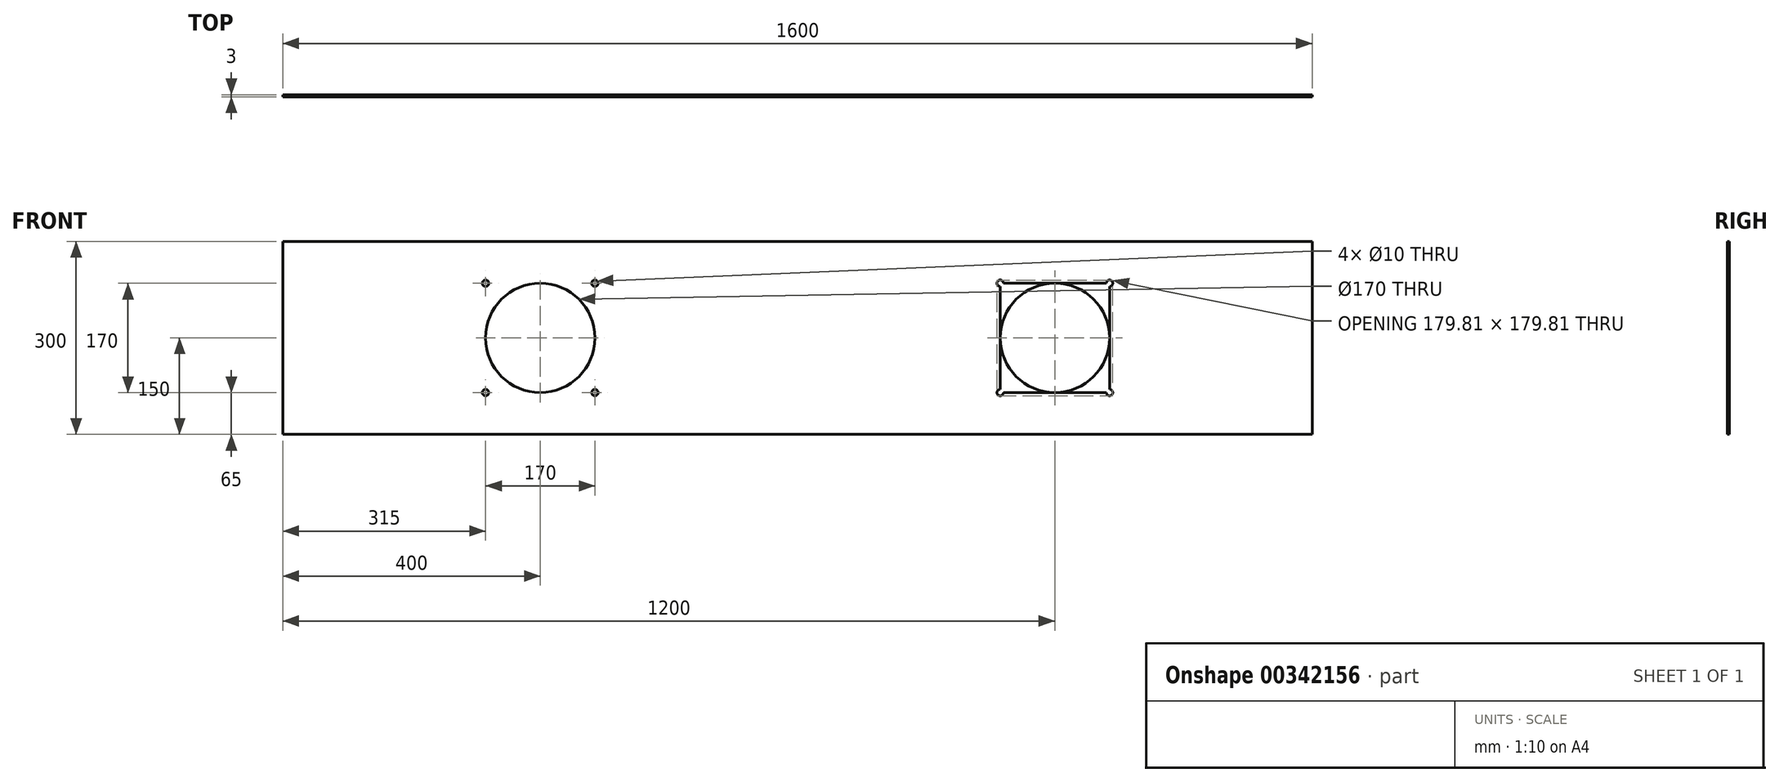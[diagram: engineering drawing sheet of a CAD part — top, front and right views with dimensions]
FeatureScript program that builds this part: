
annotation { "Feature Type Name" : "Feature", "Feature Type Description" : "" }
export const myFeature = defineFeature(function(context is Context, id is Id, definition is map)
    precondition{}
    {
        {
            var Q0;
            Q0=qCreatedBy(makeId("Front.planeOp"),FACE);
            var sketch = newSketch(context, id + "F0", { "sketchPlane" : qUnion([Q0])});
            skLineSegment(sketch, "E0.bottom", {"start": v(-800, 150) * mm, "end": v(800, 150) * mm});
            skLineSegment(sketch, "E0.top", {"start": v(-800, -150) * mm, "end": v(800, -150) * mm});
            skLineSegment(sketch, "E0.left", {"start": v(-800, 150) * mm, "end": v(-800, -150) * mm});
            skLineSegment(sketch, "E0.right", {"start": v(800, 150) * mm, "end": v(800, -150) * mm});
            skPoint(sketch, "E0.middle", {"position": v(0, 0) * mm});
            skCircle(sketch, "E1", {"center": v(-400, 0) * mm, "radius": 85 * mm});
            skCircle(sketch, "E2.MirrorC", {"center": v(400, 0) * mm, "radius": 85 * mm});
            skLineSegment(sketch, "E3.bottom", {"start": v(-315, 85) * mm, "end": v(-485, 85) * mm});
            skLineSegment(sketch, "E3.top", {"start": v(-315, -85) * mm, "end": v(-485, -85) * mm});
            skLineSegment(sketch, "E3.left", {"start": v(-315, 85) * mm, "end": v(-315, -85) * mm});
            skLineSegment(sketch, "E3.right", {"start": v(-485, 85) * mm, "end": v(-485, -85) * mm});
            skLineSegment(sketch, "E4.bottom", {"start": v(485, 85) * mm, "end": v(315, 85) * mm});
            skLineSegment(sketch, "E4.top", {"start": v(485, -85) * mm, "end": v(315, -85) * mm});
            skLineSegment(sketch, "E4.left", {"start": v(485, 85) * mm, "end": v(485, -85) * mm});
            skLineSegment(sketch, "E4.right", {"start": v(315, 85) * mm, "end": v(315, -85) * mm});
            skCircle(sketch, "E5", {"center": v(-485, 85) * mm, "radius": 5 * mm});
            skCircle(sketch, "E6", {"center": v(-315, 85) * mm, "radius": 5 * mm});
            skCircle(sketch, "E7", {"center": v(-485, -85) * mm, "radius": 5 * mm});
            skCircle(sketch, "E8", {"center": v(-315, -85) * mm, "radius": 5 * mm});
            skCircle(sketch, "E9", {"center": v(315, 85) * mm, "radius": 5 * mm});
            skCircle(sketch, "E10", {"center": v(485, 85) * mm, "radius": 5 * mm});
            skCircle(sketch, "E11", {"center": v(315, -85) * mm, "radius": 5 * mm});
            skCircle(sketch, "E12", {"center": v(485, -85) * mm, "radius": 5 * mm});
            skSolve(sketch);
        }
        {
            var Q0;
            Q0=makeQuery(id+"F0.imprint","IMPRINT",FACE,{"disambiguationData":[TD([[makeQuery(id+"F0.imprint","IMPRINT",EDGE,{"derivedFrom":sQuery(id+"F0.wireOp",EDGE,"E0.bottom")}),-1.0]])]});
            var Q1;
            {var subQ0=sQuery(id+"F0.wireOp",EDGE,"E3.bottom");var subQ1=sQuery(id+"F0.wireOp",EDGE,"E1");var subQ2=makeQuery(id+"F0.imprint","INTERSECT",VERTEX,{"derivedFrom":[subQ1,subQ0]});Q1=makeQuery(id+"F0.imprint","IMPRINT",FACE,{"disambiguationData":[TD([[makeQuery(id+"F0.imprint","IMPRINT",EDGE,{"disambiguationData":[TD([[subQ2,-1.0]])],"derivedFrom":subQ1}),-1.0]])]});}
            var Q2;
            {var subQ0=sQuery(id+"F0.wireOp",EDGE,"E3.bottom");var subQ1=sQuery(id+"F0.wireOp",EDGE,"E1");var subQ2=makeQuery(id+"F0.imprint","INTERSECT",VERTEX,{"derivedFrom":[subQ1,subQ0]});Q2=makeQuery(id+"F0.imprint","IMPRINT",FACE,{"disambiguationData":[TD([[makeQuery(id+"F0.imprint","IMPRINT",EDGE,{"disambiguationData":[TD([[subQ2,1.0]])],"derivedFrom":subQ1}),-1.0]])]});}
            var Q3;
            {var subQ0=sQuery(id+"F0.wireOp",EDGE,"E3.right");var subQ1=sQuery(id+"F0.wireOp",EDGE,"E1");var subQ2=makeQuery(id+"F0.imprint","INTERSECT",VERTEX,{"derivedFrom":[subQ1,subQ0]});Q3=makeQuery(id+"F0.imprint","IMPRINT",FACE,{"disambiguationData":[TD([[makeQuery(id+"F0.imprint","IMPRINT",EDGE,{"disambiguationData":[TD([[subQ2,-1.0]])],"derivedFrom":subQ1}),-1.0]])]});}
            var Q4;
            {var subQ0=sQuery(id+"F0.wireOp",EDGE,"E3.left");var subQ1=sQuery(id+"F0.wireOp",EDGE,"E1");var subQ2=makeQuery(id+"F0.imprint","INTERSECT",VERTEX,{"derivedFrom":[subQ1,subQ0]});Q4=makeQuery(id+"F0.imprint","IMPRINT",FACE,{"disambiguationData":[TD([[makeQuery(id+"F0.imprint","IMPRINT",EDGE,{"disambiguationData":[TD([[subQ2,1.0]])],"derivedFrom":subQ1}),-1.0]])]});}
            var Q5;
            {var subQ0=sQuery(id+"F0.wireOp",EDGE,"E4.bottom");var subQ1=sQuery(id+"F0.wireOp",EDGE,"E2.MirrorC");var subQ2=makeQuery(id+"F0.imprint","INTERSECT",VERTEX,{"derivedFrom":[subQ1,subQ0]});Q5=makeQuery(id+"F0.imprint","IMPRINT",FACE,{"disambiguationData":[TD([[makeQuery(id+"F0.imprint","IMPRINT",EDGE,{"disambiguationData":[TD([[subQ2,1.0]])],"derivedFrom":subQ1}),1.0]])]});}
            var Q6;
            {var subQ0=sQuery(id+"F0.wireOp",EDGE,"E4.bottom");var subQ1=sQuery(id+"F0.wireOp",EDGE,"E2.MirrorC");var subQ2=makeQuery(id+"F0.imprint","INTERSECT",VERTEX,{"derivedFrom":[subQ1,subQ0]});Q6=makeQuery(id+"F0.imprint","IMPRINT",FACE,{"disambiguationData":[TD([[makeQuery(id+"F0.imprint","IMPRINT",EDGE,{"disambiguationData":[TD([[subQ2,-1.0]])],"derivedFrom":subQ1}),1.0]])]});}
            var Q7;
            {var subQ0=sQuery(id+"F0.wireOp",EDGE,"E4.right");var subQ1=sQuery(id+"F0.wireOp",EDGE,"E2.MirrorC");var subQ2=makeQuery(id+"F0.imprint","INTERSECT",VERTEX,{"derivedFrom":[subQ1,subQ0]});Q7=makeQuery(id+"F0.imprint","IMPRINT",FACE,{"disambiguationData":[TD([[makeQuery(id+"F0.imprint","IMPRINT",EDGE,{"disambiguationData":[TD([[subQ2,1.0]])],"derivedFrom":subQ1}),1.0]])]});}
            var Q8;
            {var subQ0=sQuery(id+"F0.wireOp",EDGE,"E4.left");var subQ1=sQuery(id+"F0.wireOp",EDGE,"E2.MirrorC");var subQ2=makeQuery(id+"F0.imprint","INTERSECT",VERTEX,{"derivedFrom":[subQ1,subQ0]});Q8=makeQuery(id+"F0.imprint","IMPRINT",FACE,{"disambiguationData":[TD([[makeQuery(id+"F0.imprint","IMPRINT",EDGE,{"disambiguationData":[TD([[subQ2,-1.0]])],"derivedFrom":subQ1}),1.0]])]});}
            extrude(context, id + "F1", {"entities" : qUnion([Q0, Q1, Q2, Q3, Q4, Q5, Q6, Q7, Q8]), "endBound" : BoundingType.SYMMETRIC, "depth" : 3 * mm});
        }
    });
